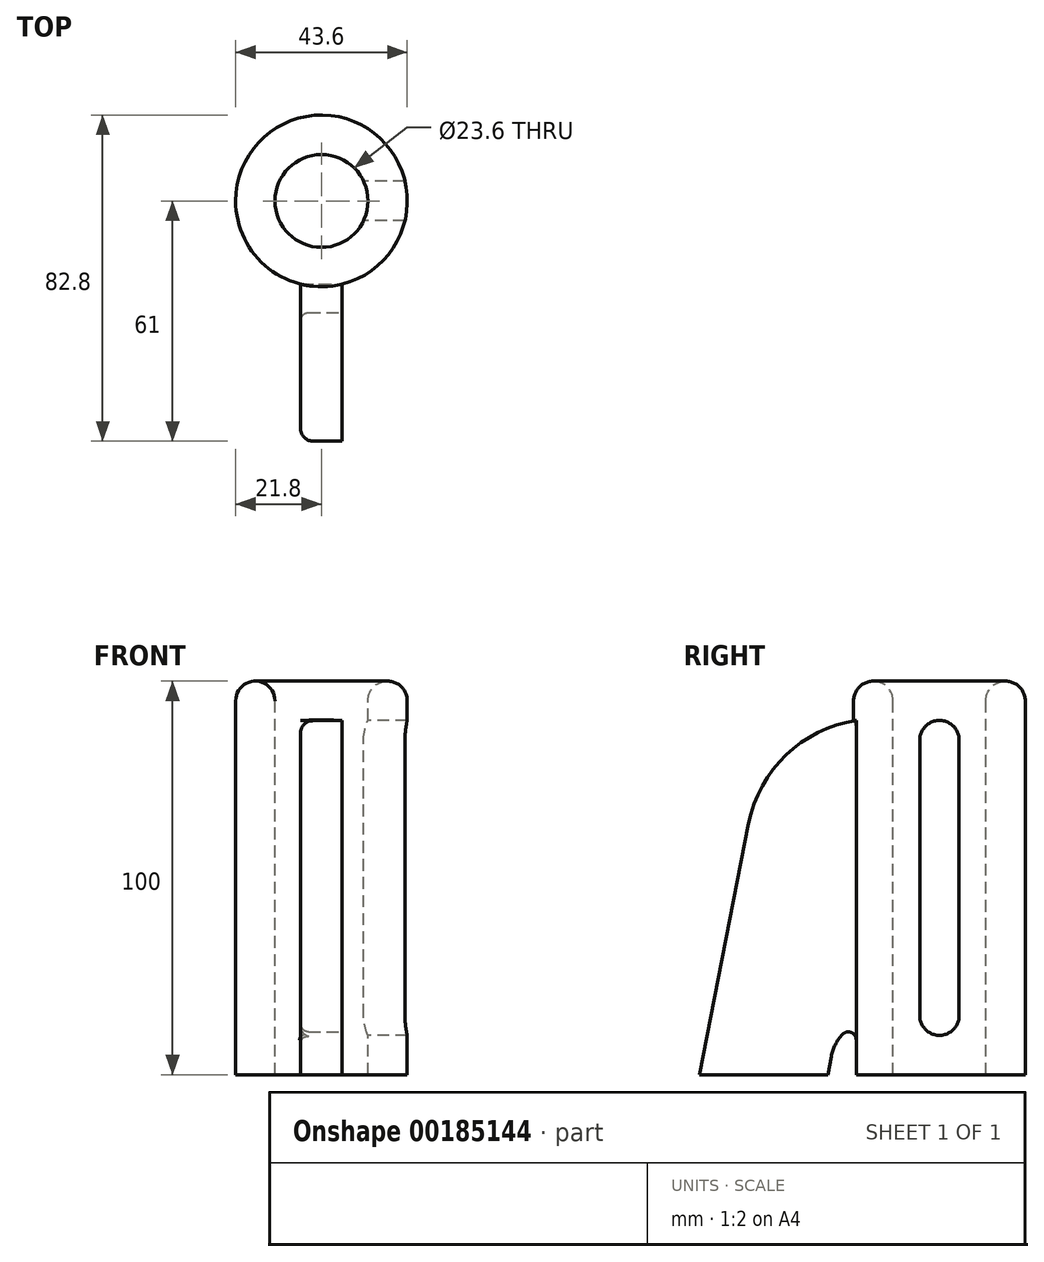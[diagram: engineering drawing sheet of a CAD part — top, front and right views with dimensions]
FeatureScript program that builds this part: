
annotation { "Feature Type Name" : "Feature", "Feature Type Description" : "" }
export const myFeature = defineFeature(function(context is Context, id is Id, definition is map)
    precondition{}
    {
        {
            var Q0;
            Q0=qCreatedBy(makeId("Front.planeOp"),FACE);
            var sketch = newSketch(context, id + "F0", { "sketchPlane" : qUnion([Q0])});
            skLineSegment(sketch, "E0", {"start": v(0, 45.68) * mm, "end": v(0, -34.36) * mm, "construction": true});
            skLineSegment(sketch, "E1.bottom", {"start": v(-21.8, 55.93) * mm, "end": v(-11.8, 55.93) * mm});
            skLineSegment(sketch, "E1.top", {"start": v(-21.8, -44.07) * mm, "end": v(-11.8, -44.07) * mm});
            skLineSegment(sketch, "E1.left", {"start": v(-21.8, 55.93) * mm, "end": v(-21.8, -44.07) * mm});
            skLineSegment(sketch, "E1.right", {"start": v(-11.8, 55.93) * mm, "end": v(-11.8, -44.07) * mm});
            skSolve(sketch);
        }
        {
            var Q0;
            Q0 = qSketchRegion(id + "F0", true);
            var Q1;
            Q1=sQuery(id+"F0.wireOp",EDGE,"E0");
            revolve(context, id + "F1", {"entities" : qUnion([Q0]), "axis" : qUnion([Q1]), "revolveType" : RevolveType.FULL});
        }
        {
            var Q0;
            Q0=qCreatedBy(makeId("Right.planeOp"),FACE);
            var sketch = newSketch(context, id + "F2", { "sketchPlane" : qUnion([Q0])});
            skLineSegment(sketch, "E2.bottom", {"start": v(-5, 45.93) * mm, "end": v(5, 45.93) * mm});
            skLineSegment(sketch, "E2.top", {"start": v(-5, -34.07) * mm, "end": v(5, -34.07) * mm});
            skLineSegment(sketch, "E2.left", {"start": v(-5, 45.93) * mm, "end": v(-5, -34.07) * mm});
            skLineSegment(sketch, "E2.right", {"start": v(5, 45.93) * mm, "end": v(5, -34.07) * mm});
            skSolve(sketch);
        }
        {
            var Q0;
            Q0=makeQuery(id+"F2.imprint","IMPRINT",FACE,{"disambiguationData":[TD([[makeQuery(id+"F2.imprint","IMPRINT",EDGE,{"derivedFrom":sQuery(id+"F2.wireOp",EDGE,"E2.bottom")}),-1.0]])]});
            extrude(context, id + "F3", {"entities" : qUnion([Q0]), "operationType" : NewBodyOperationType.REMOVE, "endBound" : BoundingType.THROUGH_ALL, "depth" : 25 * mm});
        }
        {
            var Q0;
            Q0=qCreatedBy(makeId("Front.planeOp"),FACE);
            cPlane(context, id + "F4", {"entities" : qUnion([Q0]), "cplaneType" : CPlaneType.OFFSET, "offset" : 21 * mm, "width" : 150 * mm, "height" : 150 * mm});
        }
        {
            var Q0;
            Q0=qCreatedBy(id+"F4.planeOp",FACE);
            var sketch = newSketch(context, id + "F5", { "sketchPlane" : qUnion([Q0])});
            skLineSegment(sketch, "E3.bottom", {"start": v(-5.28, 45.93) * mm, "end": v(5.28, 45.93) * mm});
            skLineSegment(sketch, "E3.top", {"start": v(-5.28, -44.07) * mm, "end": v(5.28, -44.07) * mm});
            skLineSegment(sketch, "E3.left", {"start": v(-5.28, 45.93) * mm, "end": v(-5.28, -44.07) * mm});
            skLineSegment(sketch, "E3.right", {"start": v(5.28, 45.93) * mm, "end": v(5.28, -44.07) * mm});
            skSolve(sketch);
        }
        {
            var Q0;
            Q0 = qSketchRegion(id + "F5", true);
            extrude(context, id + "F6", {"entities" : qUnion([Q0]), "operationType" : NewBodyOperationType.ADD, "depth" : 40 * mm});
        }
        {
            var Q0;
            Q0=makeQuery(id+"F6.opExtrude","SWEPT_FACE",FACE,{"disambiguationData":[OSD([sQuery(id+"F5.wireOp",EDGE,"E3.right")])]});
            var sketch = newSketch(context, id + "F7", { "sketchPlane" : qUnion([Q0])});
            skLineSegment(sketch, "E4", {"start": v(-61, -44.07) * mm, "end": v(-48.48, 19.7) * mm});
            skArc(sketch, "E5", {"start": v(-48.48, 19.7) * mm, "mid": v(-38.96, 37.14) * mm, "end": v(-21.15, 45.93) * mm});
            skLineSegment(sketch, "E6", {"start": v(-61, -44.07) * mm, "end": v(-61, -51.4) * mm});
            skLineSegment(sketch, "E7", {"start": v(-61, -51.4) * mm, "end": v(-29.83, -51.4) * mm});
            skLineSegment(sketch, "E8", {"start": v(-29.83, -51.4) * mm, "end": v(-27.49, -39.47) * mm});
            skArc(sketch, "E9", {"start": v(-27.49, -39.47) * mm, "mid": v(-25.29, -34.63) * mm, "end": v(-21.15, -31.28) * mm});
            skLineSegment(sketch, "E10", {"start": v(-21.15, -31.28) * mm, "end": v(-21.15, -61.56) * mm});
            skLineSegment(sketch, "E11", {"start": v(-21.15, -61.56) * mm, "end": v(-72.76, -61.56) * mm});
            skLineSegment(sketch, "E12", {"start": v(-72.76, -61.56) * mm, "end": v(-67.58, 53.32) * mm});
            skLineSegment(sketch, "E13", {"start": v(-67.58, 53.32) * mm, "end": v(-21.15, 45.93) * mm});
            skSolve(sketch);
        }
        {
            var Q0;
            Q0 = qSketchRegion(id + "F7", true);
            extrude(context, id + "F8", {"entities" : qUnion([Q0]), "operationType" : NewBodyOperationType.REMOVE, "endBound" : BoundingType.THROUGH_ALL, "oppositeDirection" : true, "depth" : 25 * mm});
        }
        {
            var Q0;
            Q0=makeQuery(id+"F1.opRevolve","SWEPT_EDGE",EDGE,{"disambiguationData":[OSD([sQuery(id+"F0.wireOp",EDGE,"E1.bottom"),sQuery(id+"F0.wireOp",EDGE,"E1.left")])]});
            fillet(context, id + "F9", {"entities" : qUnion([Q0]), "radius" : 5 * mm, "tangentPropagation" : true, "allowEdgeOverflow" : false});
        }
        {
            var Q0;
            Q0=makeQuery(id+"F8.boolean.opBoolean","COPY",EDGE,{"derivedFrom":makeQuery(id+"F8.opExtrude","SWEPT_EDGE",EDGE,{"disambiguationData":[OSD([sQuery(id+"F7.wireOp",EDGE,"E9"),sQuery(id+"F7.wireOp",EDGE,"E10")])]})});
            var Q1;
            Q1=makeQuery(id+"FMiiFFJCUTZdA5e_1.2.F8.boolean.opBoolean","COPY",EDGE,{"derivedFrom":makeQuery(id+"FMiiFFJCUTZdA5e_1.2.F8.opExtrude","SWEPT_EDGE",EDGE,{"disambiguationData":[OSD([sQuery(id+"F7.wireOp",EDGE,"E9"),sQuery(id+"F7.wireOp",EDGE,"E10")])]})});
            var Q2;
            Q2=makeQuery(id+"FMiiFFJCUTZdA5e_1.1.F8.boolean.opBoolean","COPY",EDGE,{"derivedFrom":makeQuery(id+"FMiiFFJCUTZdA5e_1.1.F8.opExtrude","SWEPT_EDGE",EDGE,{"disambiguationData":[OSD([sQuery(id+"F7.wireOp",EDGE,"E9"),sQuery(id+"F7.wireOp",EDGE,"E10")])]})});
            fillet(context, id + "F10", {"entities" : qUnion([Q0, Q1, Q2]), "radius" : 2 * mm, "tangentPropagation" : true, "allowEdgeOverflow" : false});
        }
        {
            var Q0;
            Q0=makeQuery(id+"Fiz973S81VzzN15_1.3.F3.boolean.opBoolean","COPY",EDGE,{"derivedFrom":makeQuery(id+"Fiz973S81VzzN15_1.3.F3.opExtrude","SWEPT_EDGE",EDGE,{"disambiguationData":[OSD([sQuery(id+"F2.wireOp",EDGE,"E2.top"),sQuery(id+"F2.wireOp",EDGE,"E2.left")])]})});
            var Q1;
            Q1=makeQuery(id+"Fiz973S81VzzN15_1.3.F3.boolean.opBoolean","COPY",EDGE,{"derivedFrom":makeQuery(id+"Fiz973S81VzzN15_1.3.F3.opExtrude","SWEPT_EDGE",EDGE,{"disambiguationData":[OSD([sQuery(id+"F2.wireOp",EDGE,"E2.top"),sQuery(id+"F2.wireOp",EDGE,"E2.right")])]})});
            var Q2;
            Q2=makeQuery(id+"Fiz973S81VzzN15_1.2.F3.boolean.opBoolean","COPY",EDGE,{"derivedFrom":makeQuery(id+"Fiz973S81VzzN15_1.2.F3.opExtrude","SWEPT_EDGE",EDGE,{"disambiguationData":[OSD([sQuery(id+"F2.wireOp",EDGE,"E2.top"),sQuery(id+"F2.wireOp",EDGE,"E2.left")])]})});
            var Q3;
            Q3=makeQuery(id+"Fiz973S81VzzN15_1.2.F3.boolean.opBoolean","COPY",EDGE,{"derivedFrom":makeQuery(id+"Fiz973S81VzzN15_1.2.F3.opExtrude","SWEPT_EDGE",EDGE,{"disambiguationData":[OSD([sQuery(id+"F2.wireOp",EDGE,"E2.top"),sQuery(id+"F2.wireOp",EDGE,"E2.right")])]})});
            var Q4;
            Q4=makeQuery(id+"Fiz973S81VzzN15_1.1.F3.boolean.opBoolean","COPY",EDGE,{"derivedFrom":makeQuery(id+"Fiz973S81VzzN15_1.1.F3.opExtrude","SWEPT_EDGE",EDGE,{"disambiguationData":[OSD([sQuery(id+"F2.wireOp",EDGE,"E2.top"),sQuery(id+"F2.wireOp",EDGE,"E2.left")])]})});
            var Q5;
            Q5=makeQuery(id+"Fiz973S81VzzN15_1.1.F3.boolean.opBoolean","COPY",EDGE,{"derivedFrom":makeQuery(id+"Fiz973S81VzzN15_1.1.F3.opExtrude","SWEPT_EDGE",EDGE,{"disambiguationData":[OSD([sQuery(id+"F2.wireOp",EDGE,"E2.top"),sQuery(id+"F2.wireOp",EDGE,"E2.right")])]})});
            var Q6;
            Q6=makeQuery(id+"F3.boolean.opBoolean","COPY",EDGE,{"derivedFrom":makeQuery(id+"F3.opExtrude","SWEPT_EDGE",EDGE,{"disambiguationData":[OSD([sQuery(id+"F2.wireOp",EDGE,"E2.top"),sQuery(id+"F2.wireOp",EDGE,"E2.right")])]})});
            var Q7;
            Q7=makeQuery(id+"F3.boolean.opBoolean","COPY",EDGE,{"derivedFrom":makeQuery(id+"F3.opExtrude","SWEPT_EDGE",EDGE,{"disambiguationData":[OSD([sQuery(id+"F2.wireOp",EDGE,"E2.top"),sQuery(id+"F2.wireOp",EDGE,"E2.left")])]})});
            var Q8;
            Q8=makeQuery(id+"Fiz973S81VzzN15_1.4.F3.boolean.opBoolean","COPY",EDGE,{"derivedFrom":makeQuery(id+"Fiz973S81VzzN15_1.4.F3.opExtrude","SWEPT_EDGE",EDGE,{"disambiguationData":[OSD([sQuery(id+"F2.wireOp",EDGE,"E2.top"),sQuery(id+"F2.wireOp",EDGE,"E2.right")])]})});
            var Q9;
            Q9=makeQuery(id+"Fiz973S81VzzN15_1.5.F3.boolean.opBoolean","COPY",EDGE,{"derivedFrom":makeQuery(id+"Fiz973S81VzzN15_1.5.F3.opExtrude","SWEPT_EDGE",EDGE,{"disambiguationData":[OSD([sQuery(id+"F2.wireOp",EDGE,"E2.top"),sQuery(id+"F2.wireOp",EDGE,"E2.left")])]})});
            var Q10;
            Q10=makeQuery(id+"Fiz973S81VzzN15_1.5.F3.boolean.opBoolean","COPY",EDGE,{"derivedFrom":makeQuery(id+"Fiz973S81VzzN15_1.5.F3.opExtrude","SWEPT_EDGE",EDGE,{"disambiguationData":[OSD([sQuery(id+"F2.wireOp",EDGE,"E2.top"),sQuery(id+"F2.wireOp",EDGE,"E2.right")])]})});
            var Q11;
            Q11=makeQuery(id+"Fiz973S81VzzN15_1.4.F3.boolean.opBoolean","COPY",EDGE,{"derivedFrom":makeQuery(id+"Fiz973S81VzzN15_1.4.F3.opExtrude","SWEPT_EDGE",EDGE,{"disambiguationData":[OSD([sQuery(id+"F2.wireOp",EDGE,"E2.top"),sQuery(id+"F2.wireOp",EDGE,"E2.left")])]})});
            var Q12;
            Q12=makeQuery(id+"Fiz973S81VzzN15_1.5.F3.boolean.opBoolean","COPY",EDGE,{"derivedFrom":makeQuery(id+"Fiz973S81VzzN15_1.5.F3.opExtrude","SWEPT_EDGE",EDGE,{"disambiguationData":[OSD([sQuery(id+"F2.wireOp",EDGE,"E2.bottom"),sQuery(id+"F2.wireOp",EDGE,"E2.right")])]})});
            var Q13;
            Q13=makeQuery(id+"F3.boolean.opBoolean","COPY",EDGE,{"derivedFrom":makeQuery(id+"F3.opExtrude","SWEPT_EDGE",EDGE,{"disambiguationData":[OSD([sQuery(id+"F2.wireOp",EDGE,"E2.bottom"),sQuery(id+"F2.wireOp",EDGE,"E2.left")])]})});
            var Q14;
            Q14=makeQuery(id+"Fiz973S81VzzN15_1.5.F3.boolean.opBoolean","COPY",EDGE,{"derivedFrom":makeQuery(id+"Fiz973S81VzzN15_1.5.F3.opExtrude","SWEPT_EDGE",EDGE,{"disambiguationData":[OSD([sQuery(id+"F2.wireOp",EDGE,"E2.bottom"),sQuery(id+"F2.wireOp",EDGE,"E2.left")])]})});
            var Q15;
            Q15=makeQuery(id+"Fiz973S81VzzN15_1.4.F3.boolean.opBoolean","COPY",EDGE,{"derivedFrom":makeQuery(id+"Fiz973S81VzzN15_1.4.F3.opExtrude","SWEPT_EDGE",EDGE,{"disambiguationData":[OSD([sQuery(id+"F2.wireOp",EDGE,"E2.bottom"),sQuery(id+"F2.wireOp",EDGE,"E2.left")])]})});
            var Q16;
            Q16=makeQuery(id+"Fiz973S81VzzN15_1.4.F3.boolean.opBoolean","COPY",EDGE,{"derivedFrom":makeQuery(id+"Fiz973S81VzzN15_1.4.F3.opExtrude","SWEPT_EDGE",EDGE,{"disambiguationData":[OSD([sQuery(id+"F2.wireOp",EDGE,"E2.bottom"),sQuery(id+"F2.wireOp",EDGE,"E2.right")])]})});
            var Q17;
            Q17=makeQuery(id+"F3.boolean.opBoolean","COPY",EDGE,{"derivedFrom":makeQuery(id+"F3.opExtrude","SWEPT_EDGE",EDGE,{"disambiguationData":[OSD([sQuery(id+"F2.wireOp",EDGE,"E2.bottom"),sQuery(id+"F2.wireOp",EDGE,"E2.right")])]})});
            var Q18;
            Q18=makeQuery(id+"Fiz973S81VzzN15_1.1.F3.boolean.opBoolean","COPY",EDGE,{"derivedFrom":makeQuery(id+"Fiz973S81VzzN15_1.1.F3.opExtrude","SWEPT_EDGE",EDGE,{"disambiguationData":[OSD([sQuery(id+"F2.wireOp",EDGE,"E2.bottom"),sQuery(id+"F2.wireOp",EDGE,"E2.right")])]})});
            var Q19;
            Q19=makeQuery(id+"Fiz973S81VzzN15_1.1.F3.boolean.opBoolean","COPY",EDGE,{"derivedFrom":makeQuery(id+"Fiz973S81VzzN15_1.1.F3.opExtrude","SWEPT_EDGE",EDGE,{"disambiguationData":[OSD([sQuery(id+"F2.wireOp",EDGE,"E2.bottom"),sQuery(id+"F2.wireOp",EDGE,"E2.left")])]})});
            var Q20;
            Q20=makeQuery(id+"Fiz973S81VzzN15_1.2.F3.boolean.opBoolean","COPY",EDGE,{"derivedFrom":makeQuery(id+"Fiz973S81VzzN15_1.2.F3.opExtrude","SWEPT_EDGE",EDGE,{"disambiguationData":[OSD([sQuery(id+"F2.wireOp",EDGE,"E2.bottom"),sQuery(id+"F2.wireOp",EDGE,"E2.right")])]})});
            var Q21;
            Q21=makeQuery(id+"Fiz973S81VzzN15_1.2.F3.boolean.opBoolean","COPY",EDGE,{"derivedFrom":makeQuery(id+"Fiz973S81VzzN15_1.2.F3.opExtrude","SWEPT_EDGE",EDGE,{"disambiguationData":[OSD([sQuery(id+"F2.wireOp",EDGE,"E2.bottom"),sQuery(id+"F2.wireOp",EDGE,"E2.left")])]})});
            var Q22;
            Q22=makeQuery(id+"Fiz973S81VzzN15_1.3.F3.boolean.opBoolean","COPY",EDGE,{"derivedFrom":makeQuery(id+"Fiz973S81VzzN15_1.3.F3.opExtrude","SWEPT_EDGE",EDGE,{"disambiguationData":[OSD([sQuery(id+"F2.wireOp",EDGE,"E2.bottom"),sQuery(id+"F2.wireOp",EDGE,"E2.right")])]})});
            var Q23;
            Q23=makeQuery(id+"Fiz973S81VzzN15_1.3.F3.boolean.opBoolean","COPY",EDGE,{"derivedFrom":makeQuery(id+"Fiz973S81VzzN15_1.3.F3.opExtrude","SWEPT_EDGE",EDGE,{"disambiguationData":[OSD([sQuery(id+"F2.wireOp",EDGE,"E2.bottom"),sQuery(id+"F2.wireOp",EDGE,"E2.left")])]})});
            fillet(context, id + "F11", {"entities" : qUnion([Q0, Q1, Q2, Q3, Q4, Q5, Q6, Q7, Q8, Q9, Q10, Q11, Q12, Q13, Q14, Q15, Q16, Q17, Q18, Q19, Q20, Q21, Q22, Q23]), "radius" : 5 * mm, "tangentPropagation" : true, "allowEdgeOverflow" : false});
        }
        {
            var Q0;
            Q0=makeQuery(id+"F1.opRevolve","SWEPT_EDGE",EDGE,{"disambiguationData":[OSD([sQuery(id+"F0.wireOp",EDGE,"E1.bottom"),sQuery(id+"F0.wireOp",EDGE,"E1.right")])]});
            fillet(context, id + "F12", {"entities" : qUnion([Q0]), "radius" : 5 * mm, "tangentPropagation" : true, "allowEdgeOverflow" : false});
        }
        {
            var Q0;
            Q0=makeQuery(id+"F8.boolean.opBoolean","COPY",EDGE,{"derivedFrom":makeQuery(id+"F8.opExtrude","CAP_EDGE",EDGE,{"disambiguationData":[OSD([sQuery(id+"F7.wireOp",EDGE,"E4")])],"isStart":true})});
            var Q1;
            Q1=makeQuery(id+"F8.boolean.opBoolean","INTERSECT",EDGE,{"derivedFrom":[makeQuery(id+"F6.opExtrude","SWEPT_FACE",FACE,{"disambiguationData":[OSD([sQuery(id+"F5.wireOp",EDGE,"E3.left")])]}),makeQuery(id+"F8.opExtrude","SWEPT_FACE",FACE,{"disambiguationData":[OSD([sQuery(id+"F7.wireOp",EDGE,"E4")])]})]});
            var Q2;
            Q2=makeQuery(id+"FMiiFFJCUTZdA5e_1.1.F8.boolean.opBoolean","COPY",EDGE,{"derivedFrom":makeQuery(id+"FMiiFFJCUTZdA5e_1.1.F8.opExtrude","CAP_EDGE",EDGE,{"disambiguationData":[OSD([sQuery(id+"F7.wireOp",EDGE,"E4")])],"isStart":true})});
            var Q3;
            Q3=makeQuery(id+"FMiiFFJCUTZdA5e_1.1.F8.boolean.opBoolean","INTERSECT",EDGE,{"derivedFrom":[makeQuery(id+"FMiiFFJCUTZdA5e_1.1.F6.opExtrude","SWEPT_FACE",FACE,{"disambiguationData":[OSD([sQuery(id+"F5.wireOp",EDGE,"E3.left")])]}),makeQuery(id+"FMiiFFJCUTZdA5e_1.1.F8.opExtrude","SWEPT_FACE",FACE,{"disambiguationData":[OSD([sQuery(id+"F7.wireOp",EDGE,"E4")])]})]});
            var Q4;
            Q4=makeQuery(id+"FMiiFFJCUTZdA5e_1.2.F8.boolean.opBoolean","COPY",EDGE,{"derivedFrom":makeQuery(id+"FMiiFFJCUTZdA5e_1.2.F8.opExtrude","CAP_EDGE",EDGE,{"disambiguationData":[OSD([sQuery(id+"F7.wireOp",EDGE,"E4")])],"isStart":true})});
            var Q5;
            Q5=makeQuery(id+"FMiiFFJCUTZdA5e_1.2.F8.boolean.opBoolean","INTERSECT",EDGE,{"derivedFrom":[makeQuery(id+"FMiiFFJCUTZdA5e_1.2.F6.opExtrude","SWEPT_FACE",FACE,{"disambiguationData":[OSD([sQuery(id+"F5.wireOp",EDGE,"E3.left")])]}),makeQuery(id+"FMiiFFJCUTZdA5e_1.2.F8.opExtrude","SWEPT_FACE",FACE,{"disambiguationData":[OSD([sQuery(id+"F7.wireOp",EDGE,"E4")])]})]});
            fillet(context, id + "F13", {"entities" : qUnion([Q0, Q1, Q2, Q3, Q4, Q5]), "radius" : 3 * mm, "tangentPropagation" : true, "allowEdgeOverflow" : false});
        }
        {
            var Q0;
            Q0=makeQuery(id+"FMiiFFJCUTZdA5e_1.1.F8.boolean.opBoolean","INTERSECT",EDGE,{"derivedFrom":[makeQuery(id+"FMiiFFJCUTZdA5e_1.1.F6.opExtrude","SWEPT_FACE",FACE,{"disambiguationData":[OSD([sQuery(id+"F5.wireOp",EDGE,"E3.left")])]}),makeQuery(id+"FMiiFFJCUTZdA5e_1.1.F8.opExtrude","SWEPT_FACE",FACE,{"disambiguationData":[OSD([sQuery(id+"F7.wireOp",EDGE,"E8")])]})]});
            var Q1;
            Q1=makeQuery(id+"FMiiFFJCUTZdA5e_1.1.F8.boolean.opBoolean","COPY",EDGE,{"derivedFrom":makeQuery(id+"FMiiFFJCUTZdA5e_1.1.F8.opExtrude","CAP_EDGE",EDGE,{"disambiguationData":[OSD([sQuery(id+"F7.wireOp",EDGE,"E8")])],"isStart":true})});
            var Q2;
            Q2=makeQuery(id+"F8.boolean.opBoolean","INTERSECT",EDGE,{"derivedFrom":[makeQuery(id+"F6.opExtrude","SWEPT_FACE",FACE,{"disambiguationData":[OSD([sQuery(id+"F5.wireOp",EDGE,"E3.left")])]}),makeQuery(id+"F8.opExtrude","SWEPT_FACE",FACE,{"disambiguationData":[OSD([sQuery(id+"F7.wireOp",EDGE,"E9")])]})]});
            var Q3;
            Q3=makeQuery(id+"F8.boolean.opBoolean","COPY",EDGE,{"derivedFrom":makeQuery(id+"F8.opExtrude","CAP_EDGE",EDGE,{"disambiguationData":[OSD([sQuery(id+"F7.wireOp",EDGE,"E8")])],"isStart":true})});
            var Q4;
            Q4=makeQuery(id+"FMiiFFJCUTZdA5e_1.2.F8.boolean.opBoolean","INTERSECT",EDGE,{"derivedFrom":[makeQuery(id+"FMiiFFJCUTZdA5e_1.2.F6.opExtrude","SWEPT_FACE",FACE,{"disambiguationData":[OSD([sQuery(id+"F5.wireOp",EDGE,"E3.left")])]}),makeQuery(id+"FMiiFFJCUTZdA5e_1.2.F8.opExtrude","SWEPT_FACE",FACE,{"disambiguationData":[OSD([sQuery(id+"F7.wireOp",EDGE,"E8")])]})]});
            var Q5;
            Q5=makeQuery(id+"FMiiFFJCUTZdA5e_1.2.F8.boolean.opBoolean","COPY",EDGE,{"derivedFrom":makeQuery(id+"FMiiFFJCUTZdA5e_1.2.F8.opExtrude","CAP_EDGE",EDGE,{"disambiguationData":[OSD([sQuery(id+"F7.wireOp",EDGE,"E9")])],"isStart":true})});
            fillet(context, id + "F14", {"entities" : qUnion([Q0, Q1, Q2, Q3, Q4, Q5]), "radius" : 2 * mm, "tangentPropagation" : true, "allowEdgeOverflow" : false});
        }
    });
